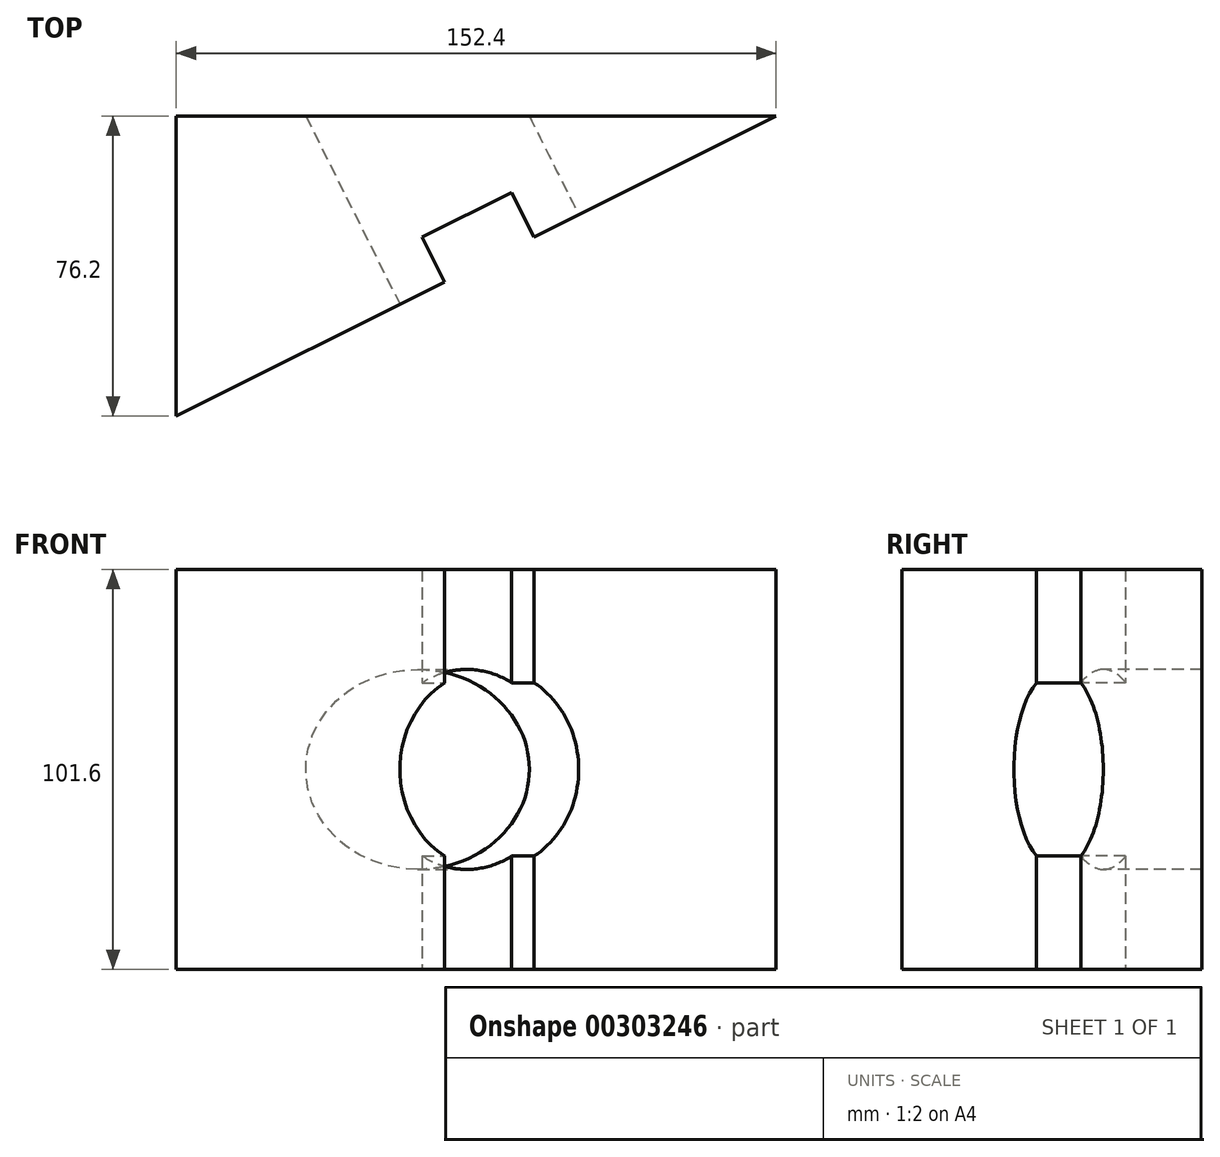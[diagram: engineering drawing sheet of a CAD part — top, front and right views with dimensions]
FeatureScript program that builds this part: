
annotation { "Feature Type Name" : "Feature", "Feature Type Description" : "" }
export const myFeature = defineFeature(function(context is Context, id is Id, definition is map)
    precondition{}
    {
        {
            var Q0;
            Q0=qCreatedBy(makeId("Top.planeOp"),FACE);
            var sketch = newSketch(context, id + "F0", { "sketchPlane" : qUnion([Q0])});
            skLineSegment(sketch, "E0.bottom", {"start": v(0, 0) * mm, "end": v(152.4, 0) * mm});
            skLineSegment(sketch, "E0.top", {"start": v(0, 76.2) * mm, "end": v(152.4, 76.2) * mm});
            skLineSegment(sketch, "E0.left", {"start": v(0, 0) * mm, "end": v(0, 76.2) * mm});
            skLineSegment(sketch, "E0.right", {"start": v(152.4, 0) * mm, "end": v(152.4, 76.2) * mm});
            skLineSegment(sketch, "E1", {"start": v(0, 0) * mm, "end": v(152.4, 76.2) * mm});
            skSolve(sketch);
        }
        {
            var Q0;
            Q0=makeQuery(id+"F0.imprint","IMPRINT",FACE,{"disambiguationData":[TD([[makeQuery(id+"F0.imprint","IMPRINT",EDGE,{"derivedFrom":sQuery(id+"F0.wireOp",EDGE,"E0.top")}),-1.0]])]});
            extrude(context, id + "F1", {"entities" : qUnion([Q0]), "depth" : 101.6 * mm});
        }
        {
            var Q0;
            Q0=makeQuery(id+"F1.opExtrude","SWEPT_FACE",FACE,{"disambiguationData":[OSD([sQuery(id+"F0.wireOp",EDGE,"E1")])]});
            var sketch = newSketch(context, id + "F2", { "sketchPlane" : qUnion([Q0])});
            skLineSegment(sketch, "E2.bottom", {"start": v(101.6, 101.6) * mm, "end": v(76.2, 101.6) * mm});
            skLineSegment(sketch, "E2.top", {"start": v(101.6, 0) * mm, "end": v(76.2, 0) * mm});
            skLineSegment(sketch, "E2.left", {"start": v(101.6, 101.6) * mm, "end": v(101.6, 0) * mm});
            skLineSegment(sketch, "E2.right", {"start": v(76.2, 101.6) * mm, "end": v(76.2, 0) * mm});
            skPoint(sketch, "E2.middle", {"position": v(88.9, 50.8) * mm});
            skSolve(sketch);
        }
        {
            var Q0;
            Q0=makeQuery(id+"F2.imprint","IMPRINT",FACE,{"disambiguationData":[TD([[makeQuery(id+"F2.imprint","IMPRINT",EDGE,{"derivedFrom":sQuery(id+"F2.wireOp",EDGE,"E2.bottom")}),-1.0]])]});
            extrude(context, id + "F3", {"entities" : qUnion([Q0]), "operationType" : NewBodyOperationType.REMOVE, "oppositeDirection" : true, "depth" : 12.7 * mm});
        }
        {
            var Q0;
            {var subQ0=sQuery(id+"F0.wireOp",EDGE,"E1");var subQ1=sQuery(id+"F0.wireOp",EDGE,"E0.left");Q0=makeQuery(id+"F3.boolean.opBoolean","SPLIT",FACE,{"disambiguationData":[TD([makeQuery(id+"F1.opExtrude","SWEPT_FACE",FACE,{"disambiguationData":[OSD([subQ1])]})])],"derivedFrom":makeQuery(id+"F1.opExtrude","SWEPT_FACE",FACE,{"disambiguationData":[OSD([subQ0])]})});}
            var sketch = newSketch(context, id + "F4", { "sketchPlane" : qUnion([Q0])});
            skCircle(sketch, "E3", {"center": v(88.93, 50.81) * mm, "radius": 25.4 * mm});
            skSolve(sketch);
        }
        {
            var Q0;
            {var subQ0=sQuery(id+"F4.wireOp",EDGE,"E3");var subQ1=makeQuery(id+"F3.boolean.opBoolean","COPY",EDGE,{"derivedFrom":makeQuery(id+"F3.opExtrude","CAP_EDGE",EDGE,{"disambiguationData":[OSD([sQuery(id+"F2.wireOp",EDGE,"E2.right")])],"isStart":true})});var subQ2=makeQuery(id+"F4.imprint","INTERSECT",VERTEX,{"disambiguationData":[OD(0.0)],"derivedFrom":[subQ1,subQ0]});Q0=makeQuery(id+"F4.imprint","IMPRINT",FACE,{"disambiguationData":[TD([[makeQuery(id+"F4.imprint","IMPRINT",EDGE,{"disambiguationData":[TD([[subQ2,1.0]])],"derivedFrom":subQ0}),1.0]])]});}
            var Q1;
            {var subQ0=sQuery(id+"F4.wireOp",EDGE,"E3");var subQ1=makeQuery(id+"F3.boolean.opBoolean","COPY",EDGE,{"derivedFrom":makeQuery(id+"F3.opExtrude","CAP_EDGE",EDGE,{"disambiguationData":[OSD([sQuery(id+"F2.wireOp",EDGE,"E2.right")])],"isStart":true})});var subQ2=makeQuery(id+"F4.imprint","INTERSECT",VERTEX,{"disambiguationData":[OD(0.0)],"derivedFrom":[subQ1,subQ0]});Q1=makeQuery(id+"F4.imprint","IMPRINT",FACE,{"disambiguationData":[TD([[makeQuery(id+"F4.imprint","IMPRINT",EDGE,{"disambiguationData":[TD([[subQ2,-1.0]])],"derivedFrom":subQ0}),1.0]])]});}
            extrude(context, id + "F5", {"entities" : qUnion([Q0, Q1]), "operationType" : NewBodyOperationType.REMOVE, "endBound" : BoundingType.THROUGH_ALL, "oppositeDirection" : true, "depth" : 25.4 * mm});
        }
    });
